# Revit family: ASSA_ABLOY_DockLeveler_DL6220ST
name_source: partatom
category: Specialty Equipment
units: mm (PartAtom-declared; Revit-internal decimal feet)

## family parameters
Always vertical = Yes
Cut with Voids When Loaded = No
Host = Floor
Part Type = Normal
Room Calculation Point = No
Round Connector Dimension = Use Diameter
Shared = No

## types (1)
- Lip LL1000
    AluminiumLip = No
    BFrame = No
    DL6220T_LipLL1000 = DL6220ST_Platform : DL6220T_LipLL1000
    DL6220T_LipLL500 = DL6220ST_Platform : DL6220T_LipLL500
    Description = Dock Leveler
    Ergo = No
    FFrame = No
    FloorThickness = 1250 mm  [stored 4.10105 ft]
    LipLength = 1000 mm  [stored 3.28084 ft]
    LipType = DL6220ST_Platform : DL6220T_LipLL1000
    Manufacturer = ASSA ABLOY
    Model = DL6220ST
    PFrame = No
    SteelLip = Yes
    TFrame = Yes
    WFrame = No

note: [stored X ft] marks values corroborated as IEEE doubles in the binary element streams (Revit-internal decimal feet)

## geometry (parser evidence)
native form markers: Sweep x22
no freeform markers — native parametric forms only
